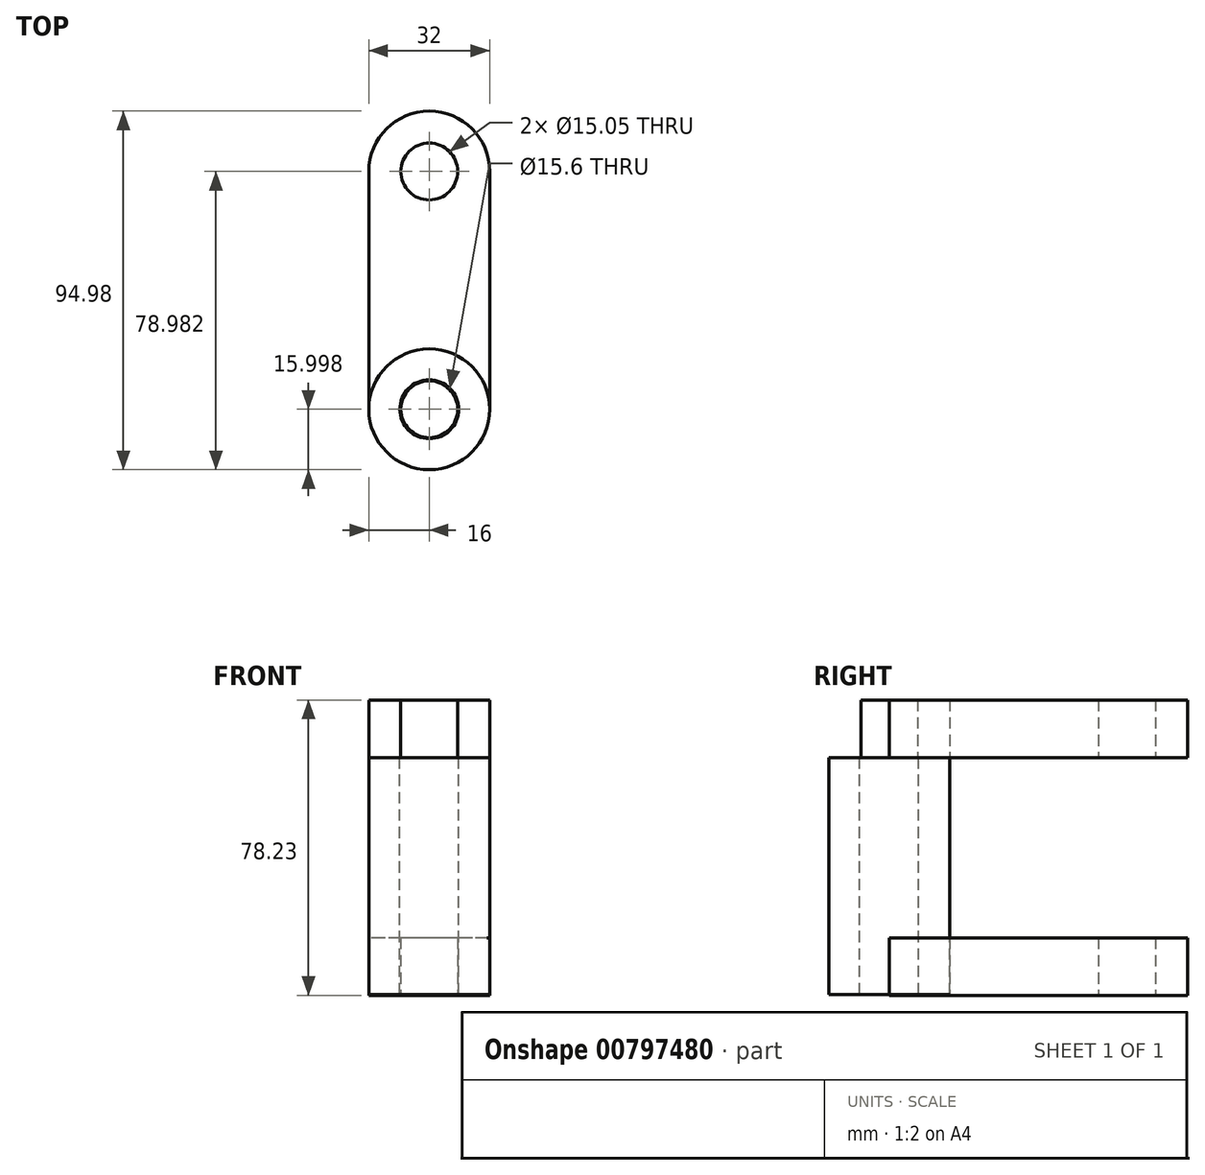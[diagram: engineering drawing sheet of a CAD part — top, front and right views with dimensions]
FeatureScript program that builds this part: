
annotation { "Feature Type Name" : "Feature", "Feature Type Description" : "" }
export const myFeature = defineFeature(function(context is Context, id is Id, definition is map)
    precondition{}
    {
        {
            var Q0;
            Q0=qCreatedBy(makeId("Top.planeOp"),FACE);
            var sketch = newSketch(context, id + "F0", { "sketchPlane" : qUnion([Q0])});
            skLineSegment(sketch, "E0.bottom", {"start": v(-16, 31.5) * mm, "end": v(16, 31.5) * mm});
            skLineSegment(sketch, "E0.top", {"start": v(-16, -31.5) * mm, "end": v(16, -31.5) * mm});
            skLineSegment(sketch, "E0.left", {"start": v(-16, 31.5) * mm, "end": v(-16, -31.5) * mm});
            skLineSegment(sketch, "E0.right", {"start": v(16, 31.5) * mm, "end": v(16, -31.5) * mm});
            skPoint(sketch, "E0.middle", {"position": v(0, 0) * mm});
            skCircle(sketch, "E1", {"center": v(0, 31.5) * mm, "radius": 16 * mm});
            skCircle(sketch, "E2", {"center": v(0, -31.5) * mm, "radius": 16 * mm});
            skCircle(sketch, "E3", {"center": v(0, 31.5) * mm, "radius": 7.53 * mm});
            skCircle(sketch, "E4.MirrorC", {"center": v(0, -31.5) * mm, "radius": 7.53 * mm});
            skSolve(sketch);
        }
        {
            var Q0;
            {var subQ1=sQuery(id+"F0.wireOp",EDGE,"E0.bottom");var subQ3=sQuery(id+"F0.wireOp",EDGE,"E3");var subQ4=makeQuery(id+"F0.imprint","INTERSECT",VERTEX,{"disambiguationData":[OD(0.0)],"derivedFrom":[subQ1,subQ3]});Q0=makeQuery(id+"F0.imprint","IMPRINT",FACE,{"disambiguationData":[TD([[makeQuery(id+"F0.imprint","IMPRINT",EDGE,{"disambiguationData":[TD([[subQ4,1.0]])],"derivedFrom":subQ3}),-1.0]])]});}
            var Q1;
            {var subQ1=sQuery(id+"F0.wireOp",EDGE,"E0.bottom");var subQ3=sQuery(id+"F0.wireOp",EDGE,"E3");var subQ4=makeQuery(id+"F0.imprint","INTERSECT",VERTEX,{"disambiguationData":[OD(0.0)],"derivedFrom":[subQ1,subQ3]});Q1=makeQuery(id+"F0.imprint","IMPRINT",FACE,{"disambiguationData":[TD([[makeQuery(id+"F0.imprint","IMPRINT",EDGE,{"disambiguationData":[TD([[subQ4,-1.0]])],"derivedFrom":subQ3}),-1.0]])]});}
            var Q2;
            {var subQ0=sQuery(id+"F0.wireOp",EDGE,"E0.left");Q2=makeQuery(id+"F0.imprint","IMPRINT",FACE,{"disambiguationData":[TD([[makeQuery(id+"F0.imprint","IMPRINT",EDGE,{"derivedFrom":subQ0}),1.0]])]});}
            var Q3;
            {var subQ0=sQuery(id+"F0.wireOp",EDGE,"E0.top");var subQ4=sQuery(id+"F0.wireOp",EDGE,"E4.MirrorC");var subQ5=makeQuery(id+"F0.imprint","INTERSECT",VERTEX,{"disambiguationData":[OD(0.0)],"derivedFrom":[subQ4,subQ0]});Q3=makeQuery(id+"F0.imprint","IMPRINT",FACE,{"disambiguationData":[TD([[makeQuery(id+"F0.imprint","IMPRINT",EDGE,{"disambiguationData":[TD([[subQ5,1.0]])],"derivedFrom":subQ4}),1.0]])]});}
            var Q4;
            {var subQ0=sQuery(id+"F0.wireOp",EDGE,"E0.top");var subQ4=sQuery(id+"F0.wireOp",EDGE,"E4.MirrorC");var subQ5=makeQuery(id+"F0.imprint","INTERSECT",VERTEX,{"disambiguationData":[OD(0.0)],"derivedFrom":[subQ4,subQ0]});Q4=makeQuery(id+"F0.imprint","IMPRINT",FACE,{"disambiguationData":[TD([[makeQuery(id+"F0.imprint","IMPRINT",EDGE,{"disambiguationData":[TD([[subQ5,-1.0]])],"derivedFrom":subQ4}),1.0]])]});}
            extrude(context, id + "F1", {"entities" : qUnion([Q0, Q1, Q2, Q3, Q4]), "depth" : 15.24 * mm, "offsetDistance" : 25.4 * mm});
        }
        {
            var Q0;
            Q0=makeQuery(id+"F1.opExtrude","SWEPT_BODY",BODY,{"disambiguationData":[OSD([sQuery(id+"F0.wireOp",EDGE,"E0.left"),sQuery(id+"F0.wireOp",EDGE,"E0.right"),sQuery(id+"F0.wireOp",EDGE,"E1"),sQuery(id+"F0.wireOp",EDGE,"E2"),sQuery(id+"F0.wireOp",EDGE,"E3"),sQuery(id+"F0.wireOp",EDGE,"E4.MirrorC")])]});
            transform(context, id + "F2", {"entities" : qUnion([Q0]), "transformType" : TransformType.TRANSLATION_3D, "dx" : 0 * mm, "dy" : 0 * mm, "dz" : -63 * mm, "makeCopy" : true});
        }
        {
            var Q0;
            Q0=makeQuery(id+"F1.opExtrude","CAP_FACE",FACE,{"disambiguationData":[OSD([sQuery(id+"F0.wireOp",EDGE,"E0.left"),sQuery(id+"F0.wireOp",EDGE,"E0.right"),sQuery(id+"F0.wireOp",EDGE,"E1"),sQuery(id+"F0.wireOp",EDGE,"E2"),sQuery(id+"F0.wireOp",EDGE,"E3"),sQuery(id+"F0.wireOp",EDGE,"E4.MirrorC")])],"isStart":true});
            var sketch = newSketch(context, id + "F3", { "sketchPlane" : qUnion([Q0])});
            skCircle(sketch, "E5", {"center": v(0, 31.5) * mm, "radius": 16 * mm});
            skCircle(sketch, "E6", {"center": v(0, 31.5) * mm, "radius": 7.8 * mm});
            skSolve(sketch);
        }
        {
            var Q0;
            Q0 = qSketchRegion(id + "F3", true);
            extrude(context, id + "F4", {"entities" : qUnion([Q0]), "depth" : 62.74 * mm, "offsetDistance" : 25.4 * mm});
        }
    });
